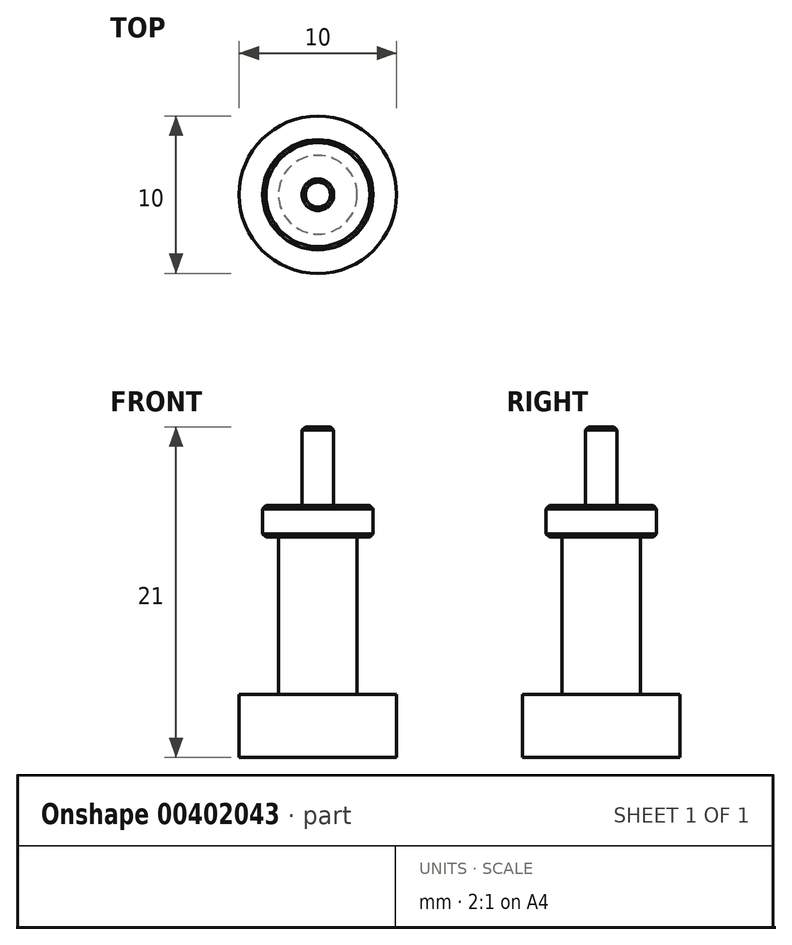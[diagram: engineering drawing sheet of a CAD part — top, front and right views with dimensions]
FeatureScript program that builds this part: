
annotation { "Feature Type Name" : "Feature", "Feature Type Description" : "" }
export const myFeature = defineFeature(function(context is Context, id is Id, definition is map)
    precondition{}
    {
        {
            var Q0;
            Q0=qCreatedBy(makeId("Top.planeOp"),FACE);
            var sketch = newSketch(context, id + "F0", { "sketchPlane" : qUnion([Q0])});
            skCircle(sketch, "E0", {"center": v(0, 0) * mm, "radius": 5 * mm});
            skSolve(sketch);
        }
        {
            var Q0;
            Q0 = qSketchRegion(id + "F0", true);
            extrude(context, id + "F1", {"entities" : qUnion([Q0]), "depth" : 4 * mm});
        }
        {
            var Q0;
            Q0=makeQuery(id+"F1.opExtrude","CAP_FACE",FACE,{"disambiguationData":[OSD([sQuery(id+"F0.wireOp",EDGE,"E0")])],"isStart":false});
            var sketch = newSketch(context, id + "F2", { "sketchPlane" : qUnion([Q0])});
            skCircle(sketch, "E1", {"center": v(0, 0) * mm, "radius": 2.5 * mm});
            skSolve(sketch);
        }
        {
            var Q0;
            Q0 = qSketchRegion(id + "F2", true);
            extrude(context, id + "F3", {"entities" : qUnion([Q0]), "operationType" : NewBodyOperationType.ADD, "depth" : 10 * mm});
        }
        {
            var Q0;
            Q0=makeQuery(id+"F3.opExtrude","CAP_FACE",FACE,{"disambiguationData":[OSD([sQuery(id+"F2.wireOp",EDGE,"E1")])],"isStart":false});
            var sketch = newSketch(context, id + "F4", { "sketchPlane" : qUnion([Q0])});
            skCircle(sketch, "E2", {"center": v(0, 0) * mm, "radius": 3.5 * mm});
            skSolve(sketch);
        }
        {
            var Q0;
            Q0 = qSketchRegion(id + "F4", true);
            extrude(context, id + "F5", {"entities" : qUnion([Q0]), "operationType" : NewBodyOperationType.ADD, "depth" : 2 * mm});
        }
        {
            var Q0;
            Q0=makeQuery(id+"F5.opExtrude","CAP_FACE",FACE,{"disambiguationData":[OSD([sQuery(id+"F4.wireOp",EDGE,"E2")])],"isStart":false});
            var sketch = newSketch(context, id + "F6", { "sketchPlane" : qUnion([Q0])});
            skCircle(sketch, "E3", {"center": v(0, 0) * mm, "radius": 1 * mm});
            skSolve(sketch);
        }
        {
            var Q0;
            Q0 = qSketchRegion(id + "F6", true);
            extrude(context, id + "F7", {"entities" : qUnion([Q0]), "operationType" : NewBodyOperationType.ADD, "depth" : 5 * mm});
        }
        {
            var Q0;
            Q0=makeQuery(id+"F7.opExtrude","CAP_EDGE",EDGE,{"disambiguationData":[OSD([sQuery(id+"F6.wireOp",EDGE,"E3")])],"isStart":false});
            var Q1;
            Q1=makeQuery(id+"F5.opExtrude","CAP_EDGE",EDGE,{"disambiguationData":[OSD([sQuery(id+"F4.wireOp",EDGE,"E2")])],"isStart":false});
            var Q2;
            Q2=makeQuery(id+"F5.opExtrude","CAP_EDGE",EDGE,{"disambiguationData":[OSD([sQuery(id+"F4.wireOp",EDGE,"E2")])],"isStart":true});
            chamfer(context, id + "F8", {"entities" : qUnion([Q0, Q1, Q2]), "width" : 0.2 * mm, "tangentPropagation" : true});
        }
    });
